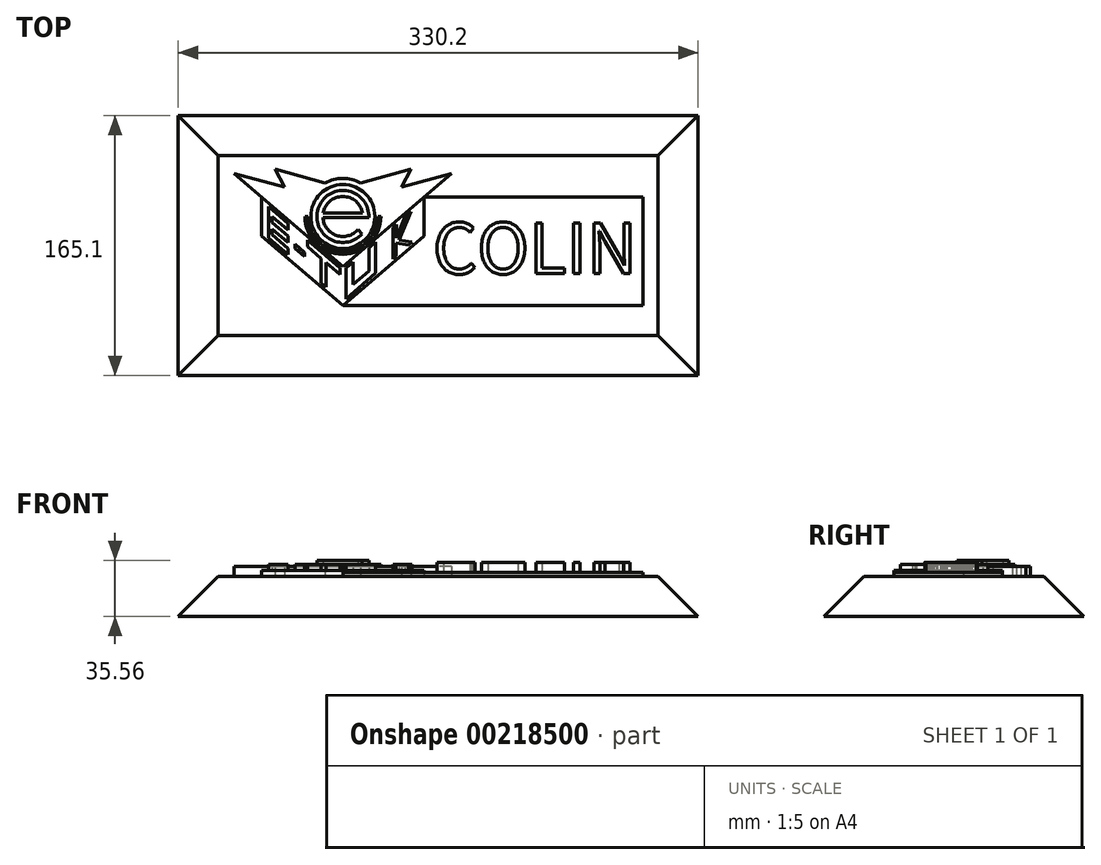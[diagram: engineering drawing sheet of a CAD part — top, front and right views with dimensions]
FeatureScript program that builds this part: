
annotation { "Feature Type Name" : "Feature", "Feature Type Description" : "" }
export const myFeature = defineFeature(function(context is Context, id is Id, definition is map)
    precondition{}
    {
        {
            var Q0;
            Q0=qCreatedBy(makeId("Top.planeOp"),FACE);
            var sketch = newSketch(context, id + "F0", { "sketchPlane" : qUnion([Q0])});
            skArc(sketch, "E0", {"start": v(12.53, 2.07) * mm, "mid": v(0, 12.7) * mm, "end": v(-12.53, 2.07) * mm});
            skArc(sketch, "E1", {"start": v(16.5, -0.78) * mm, "mid": v(-15.23, 6.37) * mm, "end": v(12.14, -11.18) * mm});
            skLineSegment(sketch, "E2", {"start": v(12.7, -0.78) * mm, "end": v(-12.68, -0.78) * mm});
            skLineSegment(sketch, "E3", {"start": v(-12.68, -0.78) * mm, "end": v(16.5, -0.78) * mm});
            skLineSegment(sketch, "E4", {"start": v(9.59, -8.33) * mm, "end": v(12.14, -11.18) * mm});
            skArc(sketch, "E5.trimOffspring", {"start": v(-12.68, -0.78) * mm, "mid": v(-4.08, -12.03) * mm, "end": v(9.59, -8.33) * mm});
            skLineSegment(sketch, "E6", {"start": v(-12.53, 2.07) * mm, "end": v(12.53, 2.07) * mm});
            skSolve(sketch);
        }
        {
            var Q0;
            Q0=makeQuery(id+"F0.imprint","IMPRINT",FACE,{"disambiguationData":[TD([[makeQuery(id+"F0.imprint","IMPRINT",EDGE,{"derivedFrom":sQuery(id+"F0.wireOp",EDGE,"E0")}),-1.0]])]});
            extrude(context, id + "F1", {"entities" : qUnion([Q0]), "depth" : 10.16 * mm});
        }
        {
            var Q0;
            Q0=qCreatedBy(makeId("Top.planeOp"),FACE);
            var sketch = newSketch(context, id + "F2", { "sketchPlane" : qUnion([Q0])});
            skCircle(sketch, "E7", {"center": v(0, 0) * mm, "radius": 20.32 * mm});
            skSolve(sketch);
        }
        {
            var Q0;
            Q0=qSketchRegion(id+"F2",true);
            extrude(context, id + "F3", {"entities" : qUnion([Q0]), "operationType" : NewBodyOperationType.ADD, "depth" : 7.62 * mm});
        }
        {
            var Q0;
            Q0=qCreatedBy(makeId("Top.planeOp"),FACE);
            var sketch = newSketch(context, id + "F4", { "sketchPlane" : qUnion([Q0])});
            skLineSegment(sketch, "E8", {"start": v(-69.02, 27.27) * mm, "end": v(-37.13, 18.72) * mm});
            skLineSegment(sketch, "E9", {"start": v(-37.13, 18.72) * mm, "end": v(-43.14, 30.14) * mm});
            skLineSegment(sketch, "E10", {"start": v(-43.14, 30.14) * mm, "end": v(-11.32, 21.31) * mm});
            skLineSegment(sketch, "E11", {"start": v(-69.02, 27.27) * mm, "end": v(0, -31.75) * mm});
            skLineSegment(sketch, "E12.MirrorCS", {"start": v(43.14, 30.14) * mm, "end": v(11.32, 21.31) * mm});
            skLineSegment(sketch, "E13.MirrorCS", {"start": v(69.02, 27.27) * mm, "end": v(0, -31.75) * mm});
            skLineSegment(sketch, "E14.MirrorCS", {"start": v(69.02, 27.27) * mm, "end": v(37.13, 18.72) * mm});
            skLineSegment(sketch, "E15.MirrorCS", {"start": v(37.13, 18.72) * mm, "end": v(43.14, 30.14) * mm});
            skArc(sketch, "E16.trimOffspring", {"start": v(11.32, 21.31) * mm, "mid": v(0, 24.13) * mm, "end": v(-11.32, 21.31) * mm});
            skSolve(sketch);
        }
        {
            var Q0;
            Q0=qSketchRegion(id+"F4",true);
            var Q1;
            Q1=makeQuery(id+"F2.imprint","IMPRINT",FACE,{"disambiguationData":[TD([[makeQuery(id+"F2.imprint","IMPRINT",EDGE,{"derivedFrom":sQuery(id+"F2.wireOp",EDGE,"E7")}),1.0]])]});
            extrude(context, id + "F5", {"entities" : qUnion([Q0, Q1]), "operationType" : NewBodyOperationType.ADD, "depth" : 6.35 * mm});
        }
        {
            var Q0;
            Q0=qCreatedBy(makeId("Top.planeOp"),FACE);
            var sketch = newSketch(context, id + "F6", { "sketchPlane" : qUnion([Q0])});
            skLineSegment(sketch, "E17", {"start": v(-51.6, -12.38) * mm, "end": v(0, -56.51) * mm});
            skLineSegment(sketch, "E18", {"start": v(0, -56.51) * mm, "end": v(51.6, -12.38) * mm});
            skLineSegment(sketch, "E19", {"start": v(-51.6, 12.38) * mm, "end": v(-51.6, -12.38) * mm});
            skLineSegment(sketch, "E20", {"start": v(51.6, 12.38) * mm, "end": v(51.6, -12.38) * mm});
            skLineSegment(sketch, "E21", {"start": v(-51.6, 12.38) * mm, "end": v(0, -31.75) * mm});
            skLineSegment(sketch, "E22", {"start": v(0, -31.75) * mm, "end": v(51.6, 12.38) * mm});
            skSolve(sketch);
        }
        {
            var Q0;
            Q0=qSketchRegion(id+"F6",true);
            extrude(context, id + "F7", {"entities" : qUnion([Q0]), "operationType" : NewBodyOperationType.ADD, "depth" : 3.8 * mm});
        }
        {
            var Q0;
            Q0=makeQuery(id+"F7.opExtrude","CAP_FACE",FACE,{"disambiguationData":[OSD([sQuery(id+"F6.wireOp",EDGE,"E17"),sQuery(id+"F6.wireOp",EDGE,"E18"),sQuery(id+"F6.wireOp",EDGE,"E19"),sQuery(id+"F6.wireOp",EDGE,"E20"),sQuery(id+"F6.wireOp",EDGE,"E21"),sQuery(id+"F6.wireOp",EDGE,"E22")])],"isStart":false});
            var sketch = newSketch(context, id + "F8", { "sketchPlane" : qUnion([Q0])});
            skPoint(sketch, "E23.startSnap0", {"position": v(-51.6, 0) * mm});
            skLineSegment(sketch, "E24", {"start": v(-51.6, -9.87) * mm, "end": v(-51.6, 9.87) * mm, "construction": true});
            skLineSegment(sketch, "E25", {"start": v(-47.26, 6.16) * mm, "end": v(-34.74, -4.55) * mm});
            skLineSegment(sketch, "E26", {"start": v(-34.74, -4.55) * mm, "end": v(-34.74, -8.63) * mm});
            skLineSegment(sketch, "E27", {"start": v(-34.74, -8.63) * mm, "end": v(-44.83, 0) * mm});
            skLineSegment(sketch, "E28", {"start": v(-44.83, 0) * mm, "end": v(-44.83, -3.75) * mm});
            skLineSegment(sketch, "E29", {"start": v(-44.83, -3.75) * mm, "end": v(-34.74, -12.38) * mm});
            skLineSegment(sketch, "E30", {"start": v(-34.74, -12.38) * mm, "end": v(-34.74, -16.46) * mm});
            skLineSegment(sketch, "E31", {"start": v(-34.74, -16.46) * mm, "end": v(-44.83, -7.83) * mm});
            skLineSegment(sketch, "E32", {"start": v(-44.83, -7.83) * mm, "end": v(-44.83, -11.58) * mm});
            skLineSegment(sketch, "E33", {"start": v(-44.83, -11.58) * mm, "end": v(-34.74, -20.21) * mm});
            skLineSegment(sketch, "E34", {"start": v(-34.74, -20.21) * mm, "end": v(-34.74, -24.3) * mm});
            skLineSegment(sketch, "E35", {"start": v(-34.74, -24.3) * mm, "end": v(-47.26, -13.59) * mm});
            skLineSegment(sketch, "E36", {"start": v(-47.26, 6.16) * mm, "end": v(-47.26, -13.59) * mm});
            skLineSegment(sketch, "E37", {"start": v(-30.38, -20.21) * mm, "end": v(-30.38, -17.65) * mm});
            skLineSegment(sketch, "E38", {"start": v(-30.38, -17.65) * mm, "end": v(-24.17, -22.96) * mm});
            skLineSegment(sketch, "E39", {"start": v(-24.17, -22.96) * mm, "end": v(-24.17, -25.53) * mm});
            skLineSegment(sketch, "E40", {"start": v(-24.17, -25.53) * mm, "end": v(-30.38, -20.21) * mm});
            skLineSegment(sketch, "E41", {"start": v(-22.38, -15.12) * mm, "end": v(-1.9, -32.63) * mm});
            skLineSegment(sketch, "E42", {"start": v(-1.9, -32.63) * mm, "end": v(-1.9, -36.71) * mm});
            skLineSegment(sketch, "E43", {"start": v(-1.9, -36.71) * mm, "end": v(-10.6, -29.28) * mm});
            skLineSegment(sketch, "E44", {"start": v(-10.6, -29.28) * mm, "end": v(-10.6, -44.95) * mm});
            skLineSegment(sketch, "E45", {"start": v(-10.6, -44.95) * mm, "end": v(-13.7, -42.3) * mm});
            skLineSegment(sketch, "E46", {"start": v(-13.7, -42.3) * mm, "end": v(-13.7, -26.63) * mm});
            skLineSegment(sketch, "E47", {"start": v(-13.7, -26.63) * mm, "end": v(-22.38, -19.2) * mm});
            skLineSegment(sketch, "E48", {"start": v(-22.38, -19.2) * mm, "end": v(-22.38, -15.12) * mm});
            skLineSegment(sketch, "E49", {"start": v(1.9, -32.62) * mm, "end": v(6.3, -28.86) * mm});
            skLineSegment(sketch, "E50", {"start": v(6.3, -28.86) * mm, "end": v(6.3, -43.26) * mm});
            skLineSegment(sketch, "E51", {"start": v(6.3, -43.26) * mm, "end": v(16.5, -34.54) * mm});
            skLineSegment(sketch, "E52", {"start": v(16.5, -34.54) * mm, "end": v(16.5, -20.14) * mm});
            skLineSegment(sketch, "E53", {"start": v(16.5, -20.14) * mm, "end": v(20.85, -16.3) * mm});
            skLineSegment(sketch, "E54", {"start": v(20.85, -16.3) * mm, "end": v(20.85, -36.06) * mm});
            skLineSegment(sketch, "E55", {"start": v(20.85, -36.06) * mm, "end": v(1.9, -52.37) * mm});
            skLineSegment(sketch, "E56", {"start": v(1.9, -52.37) * mm, "end": v(1.9, -32.62) * mm});
            skLineSegment(sketch, "E57", {"start": v(31.73, -7.12) * mm, "end": v(31.73, -27.15) * mm});
            skLineSegment(sketch, "E58", {"start": v(31.73, -27.15) * mm, "end": v(33.91, -25.22) * mm});
            skLineSegment(sketch, "E59", {"start": v(33.91, -25.22) * mm, "end": v(33.91, -16.82) * mm});
            skLineSegment(sketch, "E60", {"start": v(33.94, -13.64) * mm, "end": v(33.94, -5.23) * mm});
            skLineSegment(sketch, "E61", {"start": v(33.94, -5.23) * mm, "end": v(31.73, -7.12) * mm});
            skLineSegment(sketch, "E62", {"start": v(41.79, -18.27) * mm, "end": v(44, -16.38) * mm});
            skLineSegment(sketch, "E63", {"start": v(33.94, -13.64) * mm, "end": v(39.5, 0) * mm});
            skLineSegment(sketch, "E64", {"start": v(33.91, -16.82) * mm, "end": v(41.79, -18.27) * mm});
            skLineSegment(sketch, "E65", {"start": v(44, -16.38) * mm, "end": v(35.85, -14.87) * mm});
            skLineSegment(sketch, "E66", {"start": v(35.85, -14.87) * mm, "end": v(43.2, 3.16) * mm});
            skLineSegment(sketch, "E67", {"start": v(39.5, 0) * mm, "end": v(43.2, 3.16) * mm});
            skSolve(sketch);
        }
        {
            var Q0;
            Q0=qSketchRegion(id+"F8",true);
            extrude(context, id + "F9", {"entities" : qUnion([Q0]), "operationType" : NewBodyOperationType.ADD, "depth" : 3.8 * mm});
        }
        {
            var Q0;
            Q0=makeQuery(id+"F5.boolean.opBoolean","MERGE",FACE,{"derivedFrom":[makeQuery(id+"F5.opExtrude","CAP_FACE",FACE,{"disambiguationData":[OSD([sQuery(id+"F2.wireOp",EDGE,"E7")])],"isStart":false}),makeQuery(id+"F5.opExtrude","CAP_FACE",FACE,{"disambiguationData":[OSD([sQuery(id+"F4.wireOp",EDGE,"E8"),sQuery(id+"F4.wireOp",EDGE,"E9"),sQuery(id+"F4.wireOp",EDGE,"E10"),sQuery(id+"F4.wireOp",EDGE,"E11"),sQuery(id+"F4.wireOp",EDGE,"E13.MirrorCS"),sQuery(id+"F4.wireOp",EDGE,"E14.MirrorCS"),sQuery(id+"F4.wireOp",EDGE,"E12.MirrorCS"),sQuery(id+"F4.wireOp",EDGE,"E15.MirrorCS"),sQuery(id+"F4.wireOp",EDGE,"E16.trimOffspring")])],"isStart":false})]});
            var sketch = newSketch(context, id + "F10", { "sketchPlane" : qUnion([Q0])});
            skArc(sketch, "E68", {"start": v(-24.13, 0) * mm, "mid": v(0, -24.13) * mm, "end": v(24.13, 0) * mm});
            skArc(sketch, "E69", {"start": v(-22.23, 0) * mm, "mid": v(0, -22.23) * mm, "end": v(22.23, 0) * mm});
            skLineSegment(sketch, "E70", {"start": v(-24.13, 0) * mm, "end": v(-22.23, 0) * mm});
            skLineSegment(sketch, "E71", {"start": v(24.13, 0) * mm, "end": v(22.23, 0) * mm});
            skSolve(sketch);
        }
        {
            var Q0;
            Q0=qSketchRegion(id+"F10",true);
            extrude(context, id + "F11", {"entities" : qUnion([Q0]), "operationType" : NewBodyOperationType.ADD, "depth" : 1.27 * mm});
        }
        {
            var Q0;
            {var subQ0=sQuery(id+"F2.wireOp",EDGE,"E7");Q0=makeQuery(id+"F7.boolean.opBoolean","MERGE",FACE,{"derivedFrom":[makeQuery(id+"F5.boolean.opBoolean","MERGE",FACE,{"derivedFrom":[makeQuery(id+"F3.boolean.opBoolean","MERGE",FACE,{"derivedFrom":[makeQuery(id+"F1.opExtrude","CAP_FACE",FACE,{"disambiguationData":[OSD([sQuery(id+"F0.wireOp",EDGE,"E0"),sQuery(id+"F0.wireOp",EDGE,"E1"),sQuery(id+"F0.wireOp",EDGE,"E3"),sQuery(id+"F0.wireOp",EDGE,"E4"),sQuery(id+"F0.wireOp",EDGE,"E5.trimOffspring"),sQuery(id+"F0.wireOp",EDGE,"E6")])],"isStart":true}),makeQuery(id+"F3.opExtrude","CAP_FACE",FACE,{"disambiguationData":[OSD([subQ0])],"isStart":true})]}),makeQuery(id+"F5.opExtrude","CAP_FACE",FACE,{"disambiguationData":[OSD([subQ0])],"isStart":true}),makeQuery(id+"F5.opExtrude","CAP_FACE",FACE,{"disambiguationData":[OSD([sQuery(id+"F4.wireOp",EDGE,"E8"),sQuery(id+"F4.wireOp",EDGE,"E9"),sQuery(id+"F4.wireOp",EDGE,"E10"),sQuery(id+"F4.wireOp",EDGE,"E11"),sQuery(id+"F4.wireOp",EDGE,"E13.MirrorCS"),sQuery(id+"F4.wireOp",EDGE,"E14.MirrorCS"),sQuery(id+"F4.wireOp",EDGE,"E12.MirrorCS"),sQuery(id+"F4.wireOp",EDGE,"E15.MirrorCS"),sQuery(id+"F4.wireOp",EDGE,"E16.trimOffspring")])],"isStart":true})]}),makeQuery(id+"F7.opExtrude","CAP_FACE",FACE,{"disambiguationData":[OSD([sQuery(id+"F6.wireOp",EDGE,"E17"),sQuery(id+"F6.wireOp",EDGE,"E18"),sQuery(id+"F6.wireOp",EDGE,"E19"),sQuery(id+"F6.wireOp",EDGE,"E20"),sQuery(id+"F6.wireOp",EDGE,"E21"),sQuery(id+"F6.wireOp",EDGE,"E22")])],"isStart":true})]});}
            var sketch = newSketch(context, id + "F12", { "sketchPlane" : qUnion([Q0])});
            skLineSegment(sketch, "E72.bottom", {"start": v(0, 56.51) * mm, "end": v(190.5, 56.51) * mm});
            skLineSegment(sketch, "E72.right", {"start": v(190.5, 56.51) * mm, "end": v(190.5, -12.38) * mm});
            skLineSegment(sketch, "E73", {"start": v(51.6, -12.38) * mm, "end": v(190.5, -12.38) * mm});
            skLineSegment(sketch, "E74", {"start": v(0, 56.51) * mm, "end": v(51.6, 12.38) * mm});
            skLineSegment(sketch, "E75", {"start": v(51.6, 12.38) * mm, "end": v(51.6, -12.38) * mm});
            skSolve(sketch);
        }
        {
            var Q0;
            Q0=qSketchRegion(id+"F12",true);
            extrude(context, id + "F13", {"entities" : qUnion([Q0]), "operationType" : NewBodyOperationType.ADD, "oppositeDirection" : true, "depth" : 2.54 * mm});
        }
        {
            var Q0;
            Q0=makeQuery(id+"F13.opExtrude","CAP_FACE",FACE,{"disambiguationData":[OSD([sQuery(id+"F12.wireOp",EDGE,"E72.bottom"),sQuery(id+"F12.wireOp",EDGE,"E72.right"),sQuery(id+"F12.wireOp",EDGE,"E73"),sQuery(id+"F12.wireOp",EDGE,"E74"),sQuery(id+"F12.wireOp",EDGE,"E75")])],"isStart":false});
            var sketch = newSketch(context, id + "F14", { "sketchPlane" : qUnion([Q0])});
            skLineSegment(sketch, "E76", {"start": v(51.6, 12.38) * mm, "end": v(51.6, -56.51) * mm, "construction": true});
            skLineSegment(sketch, "E77", {"start": v(51.6, -56.51) * mm, "end": v(190.5, -56.51) * mm, "construction": true});
            skLineSegment(sketch, "E78", {"start": v(190.5, -56.51) * mm, "end": v(190.5, 12.38) * mm, "construction": true});
            skLineSegment(sketch, "E79", {"start": v(190.5, 12.38) * mm, "end": v(51.6, 12.38) * mm, "construction": true});
            skPoint(sketch, "E80.startSnap0", {"position": v(51.6, 0) * mm});
            skPoint(sketch, "E80.endSnap0", {"position": v(51.6, 0) * mm});
            skLineSegment(sketch, "E81", {"start": v(184.83, -36.36) * mm, "end": v(57.26, -36.36) * mm, "construction": true});
            skLineSegment(sketch, "E82", {"start": v(178.12, -4.6) * mm, "end": v(57.26, -4.6) * mm, "construction": true});
            skText(sketch, "E83", { "text": "COLIN", "fontName": "NotoSansCJKkr-Regular.otf"});
            const initialGuessF14  = {"E83": [0.05726, -0.03636, 1, 0, 0.03175]};
            skSetInitialGuess(sketch, initialGuessF14);
            skSolve(sketch);
        }
        {
            var Q0;
            Q0=qSketchRegion(id+"F14",true);
            extrude(context, id + "F15", {"entities" : qUnion([Q0]), "operationType" : NewBodyOperationType.ADD, "depth" : 6.35 * mm});
        }
        {
            var Q0;
            Q0=makeQuery(id+"F13.opExtrude","CAP_FACE",FACE,{"disambiguationData":[OSD([sQuery(id+"F12.wireOp",EDGE,"E72.bottom"),sQuery(id+"F12.wireOp",EDGE,"E72.right"),sQuery(id+"F12.wireOp",EDGE,"E73"),sQuery(id+"F12.wireOp",EDGE,"E74"),sQuery(id+"F12.wireOp",EDGE,"E75")])],"isStart":true});
            var sketch = newSketch(context, id + "F16", { "sketchPlane" : qUnion([Q0])});
            skLineSegment(sketch, "E84.bottom", {"start": v(-79.18, -38.74) * mm, "end": v(200.22, -38.74) * mm});
            skLineSegment(sketch, "E84.top", {"start": v(-79.18, 75.56) * mm, "end": v(200.22, 75.56) * mm});
            skLineSegment(sketch, "E84.left", {"start": v(-79.18, -38.74) * mm, "end": v(-79.18, 75.56) * mm});
            skLineSegment(sketch, "E84.right", {"start": v(200.22, -38.74) * mm, "end": v(200.22, 75.56) * mm});
            skSolve(sketch);
        }
        {
            var Q0;
            Q0=qSketchRegion(id+"F16",true);
            extrude(context, id + "F17", {"entities" : qUnion([Q0]), "operationType" : NewBodyOperationType.ADD, "depth" : 25.4 * mm, "hasDraft" : true, "draftAngle" : 45 * degree});
        }
    });
